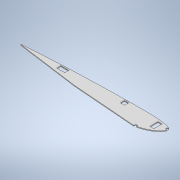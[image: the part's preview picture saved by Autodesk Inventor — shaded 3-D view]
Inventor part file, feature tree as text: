
AUTODESK INVENTOR PART (.ipt)
format: ipt  version: 2021 (Build 250183000, 183)  size: 182,272 bytes
history: native  units: mm
features: extrude x1, sketch x1
ambient origin geometry x8: Origin, YZ Plane, XZ Plane, XY Plane, X Axis, Y Axis, Z Axis, Center Point
bodies: Body1 (feature_tree)
feature tree (2):
  extrude  "Extrusion3"  Depth=10.0mm
  sketch  "Sketch1"  dims[d5=160.0mm d8=160.0mm d10=18.5mm d11=10.0mm d12=20.0mm d13=20.0mm d14=10.0mm d17=5.0mm d18=5.0mm d25=6.0mm d26=5.0mm d27=5.0mm d28=2.0mm d29=0.0mm d30=17.227785mm d31=34.456mm d33=10.0mm d34=10.0mm d35=15.0mm d36=5.0mm d37=5.0mm d40=23.0mm d41=25.0mm d42=10.0mm d43=10.0mm d47=115.0mm d48=18.5mm d49=104.485399mm d50=368.759386mm]
